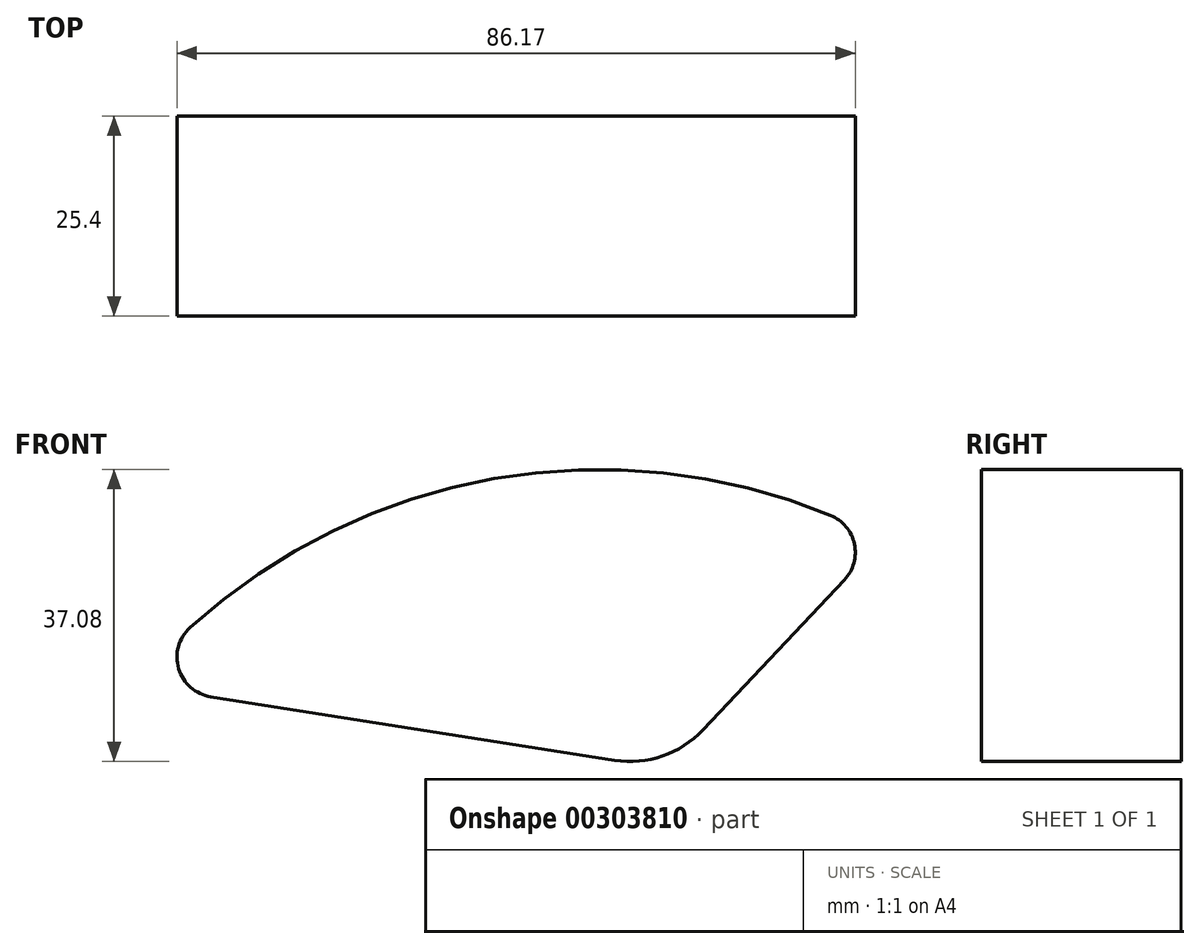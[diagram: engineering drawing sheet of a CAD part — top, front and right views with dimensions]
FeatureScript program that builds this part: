
annotation { "Feature Type Name" : "Feature", "Feature Type Description" : "" }
export const myFeature = defineFeature(function(context is Context, id is Id, definition is map)
    precondition{}
    {
        {
            var Q0;
            Q0=qCreatedBy(makeId("Front.planeOp"),FACE);
            var sketch = newSketch(context, id + "F0", { "sketchPlane" : qUnion([Q0])});
            skLineSegment(sketch, "E0", {"start": v(37.12, 49.8) * mm, "end": v(14.33, 25.62) * mm});
            skLineSegment(sketch, "E1", {"start": v(3.12, 21.78) * mm, "end": v(-57.83, 31.36) * mm});
            skArc(sketch, "E2", {"start": v(37.12, 49.8) * mm, "mid": v(-13.6, 57.3) * mm, "end": v(-57.83, 31.36) * mm});
            skPoint(sketch, "E3.visualSharp", {"position": v(9.73, 20.74) * mm});
            skArc(sketch, "E3.filletArc", {"start": v(3.12, 21.78) * mm, "mid": v(9.2, 22.31) * mm, "end": v(14.33, 25.62) * mm});
            skSolve(sketch);
        }
        {
            var Q0;
            Q0=makeQuery(id+"F0.imprint","IMPRINT",FACE,{"disambiguationData":[TD([[makeQuery(id+"F0.imprint","IMPRINT",EDGE,{"derivedFrom":sQuery(id+"F0.wireOp",EDGE,"E0")}),-1.0]])]});
            extrude(context, id + "F1", {"entities" : qUnion([Q0]), "depth" : 25.4 * mm});
        }
        {
            var Q0;
            Q0=makeQuery(id+"F1.opExtrude","SWEPT_EDGE",EDGE,{"disambiguationData":[OSD([sQuery(id+"F0.wireOp",EDGE,"E1"),sQuery(id+"F0.wireOp",EDGE,"E2")])]});
            var Q1;
            Q1=makeQuery(id+"F1.opExtrude","SWEPT_EDGE",EDGE,{"disambiguationData":[OSD([sQuery(id+"F0.wireOp",EDGE,"E0"),sQuery(id+"F0.wireOp",EDGE,"E2")])]});
            fillet(context, id + "F2", {"entities" : qUnion([Q0, Q1]), "radius" : 5.08 * mm, "tangentPropagation" : true, "allowEdgeOverflow" : false});
        }
    });
